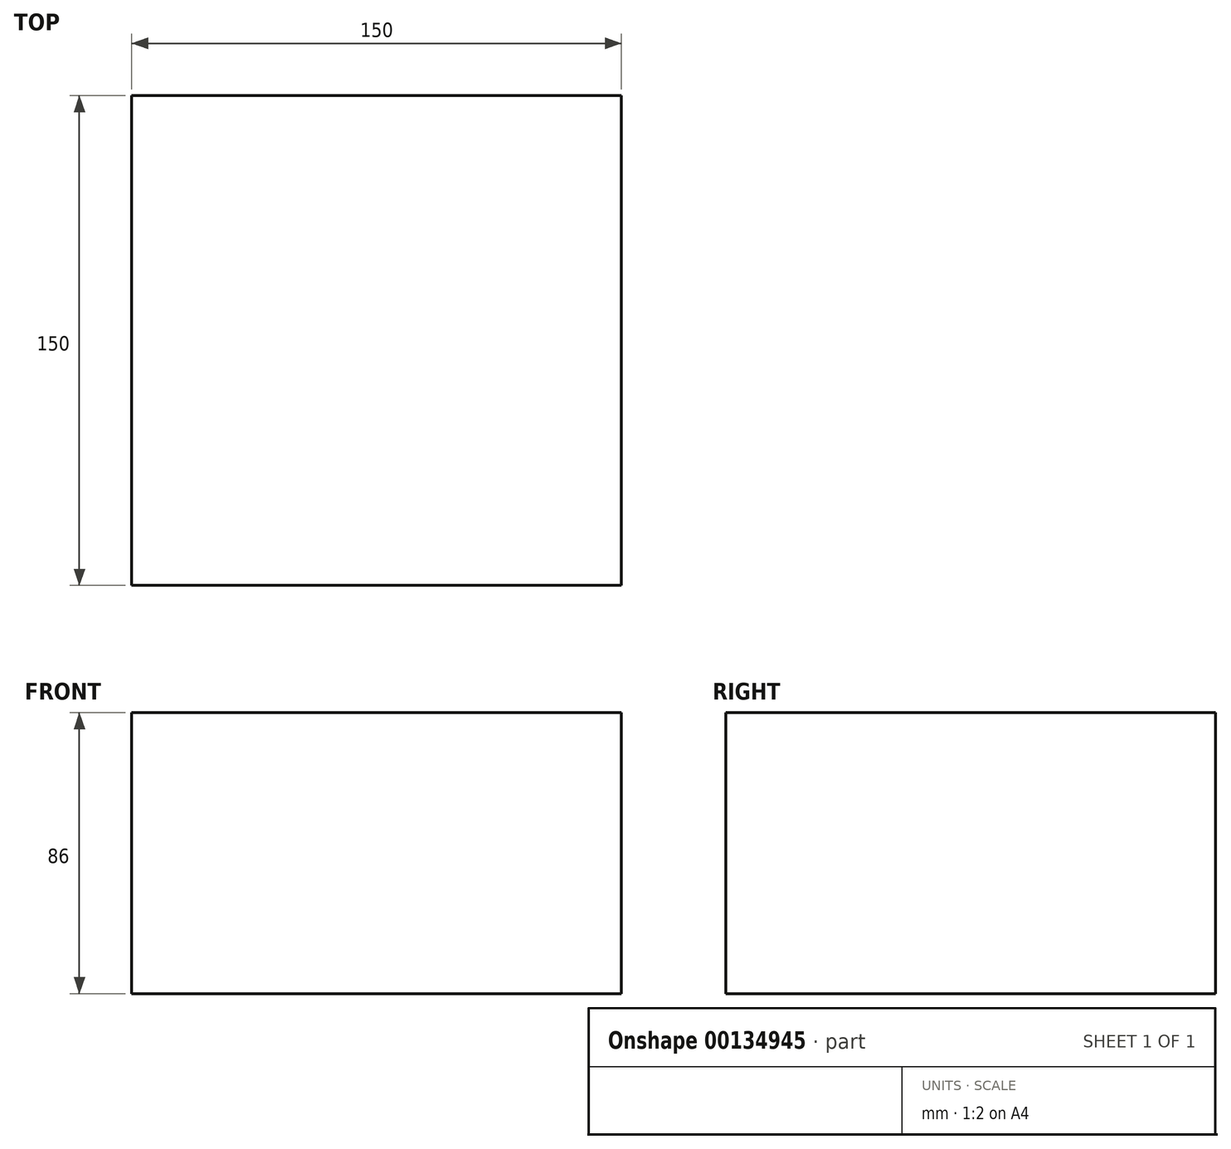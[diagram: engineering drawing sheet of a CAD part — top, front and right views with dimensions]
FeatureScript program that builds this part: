
annotation { "Feature Type Name" : "Feature", "Feature Type Description" : "" }
export const myFeature = defineFeature(function(context is Context, id is Id, definition is map)
    precondition{}
    {
        {
            var Q0;
            Q0=qCreatedBy(makeId("Front.planeOp"),FACE);
            var sketch = newSketch(context, id + "F0", { "sketchPlane" : qUnion([Q0])});
            skLineSegment(sketch, "E0.bottom", {"start": v(0, 0) * mm, "end": v(150, 0) * mm});
            skLineSegment(sketch, "E0.top", {"start": v(0, 86) * mm, "end": v(150, 86) * mm});
            skLineSegment(sketch, "E0.left", {"start": v(0, 0) * mm, "end": v(0, 86) * mm});
            skLineSegment(sketch, "E0.right", {"start": v(150, 0) * mm, "end": v(150, 86) * mm});
            skSolve(sketch);
        }
        {
            var Q0;
            Q0=makeQuery(id+"F0.imprint","IMPRINT",FACE,{"disambiguationData":[TD([[makeQuery(id+"F0.imprint","IMPRINT",EDGE,{"derivedFrom":sQuery(id+"F0.wireOp",EDGE,"E0.bottom")}),1.0]])]});
            extrude(context, id + "F1", {"entities" : qUnion([Q0]), "depth" : 150 * mm});
        }
    });
